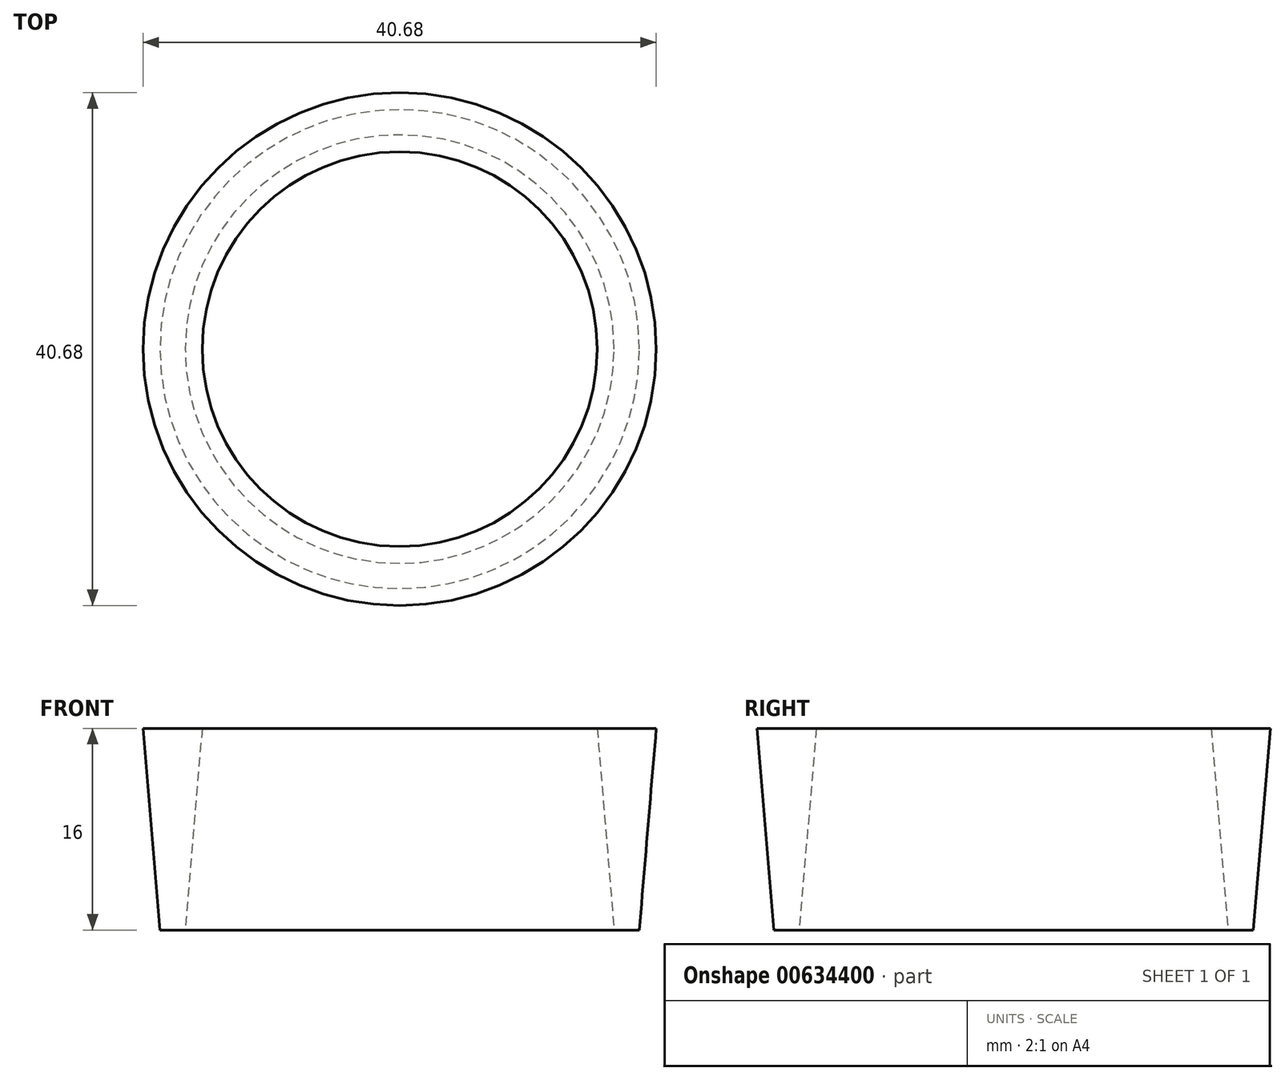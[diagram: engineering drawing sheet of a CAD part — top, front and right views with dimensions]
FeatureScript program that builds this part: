
annotation { "Feature Type Name" : "Feature", "Feature Type Description" : "" }
export const myFeature = defineFeature(function(context is Context, id is Id, definition is map)
    precondition{}
    {
        {
            var Q0;
            Q0=qCreatedBy(makeId("Top.planeOp"),FACE);
            var sketch = newSketch(context, id + "F0", { "sketchPlane" : qUnion([Q0])});
            skCircle(sketch, "E0", {"center": v(0, 0) * mm, "radius": 19 * mm});
            skCircle(sketch, "E1", {"center": v(0, 0) * mm, "radius": 17 * mm});
            skSolve(sketch);
        }
        {
            var Q0;
            Q0=makeQuery(id+"F0.imprint","IMPRINT",FACE,{"disambiguationData":[TD([[makeQuery(id+"F0.imprint","IMPRINT",EDGE,{"derivedFrom":sQuery(id+"F0.wireOp",EDGE,"E0")}),1.0]])]});
            extrude(context, id + "F1", {"entities" : qUnion([Q0]), "depth" : 16 * mm, "offsetDistance" : 25 * mm, "hasDraft" : true, "draftAngle" : 4.8 * degree});
        }
    });
